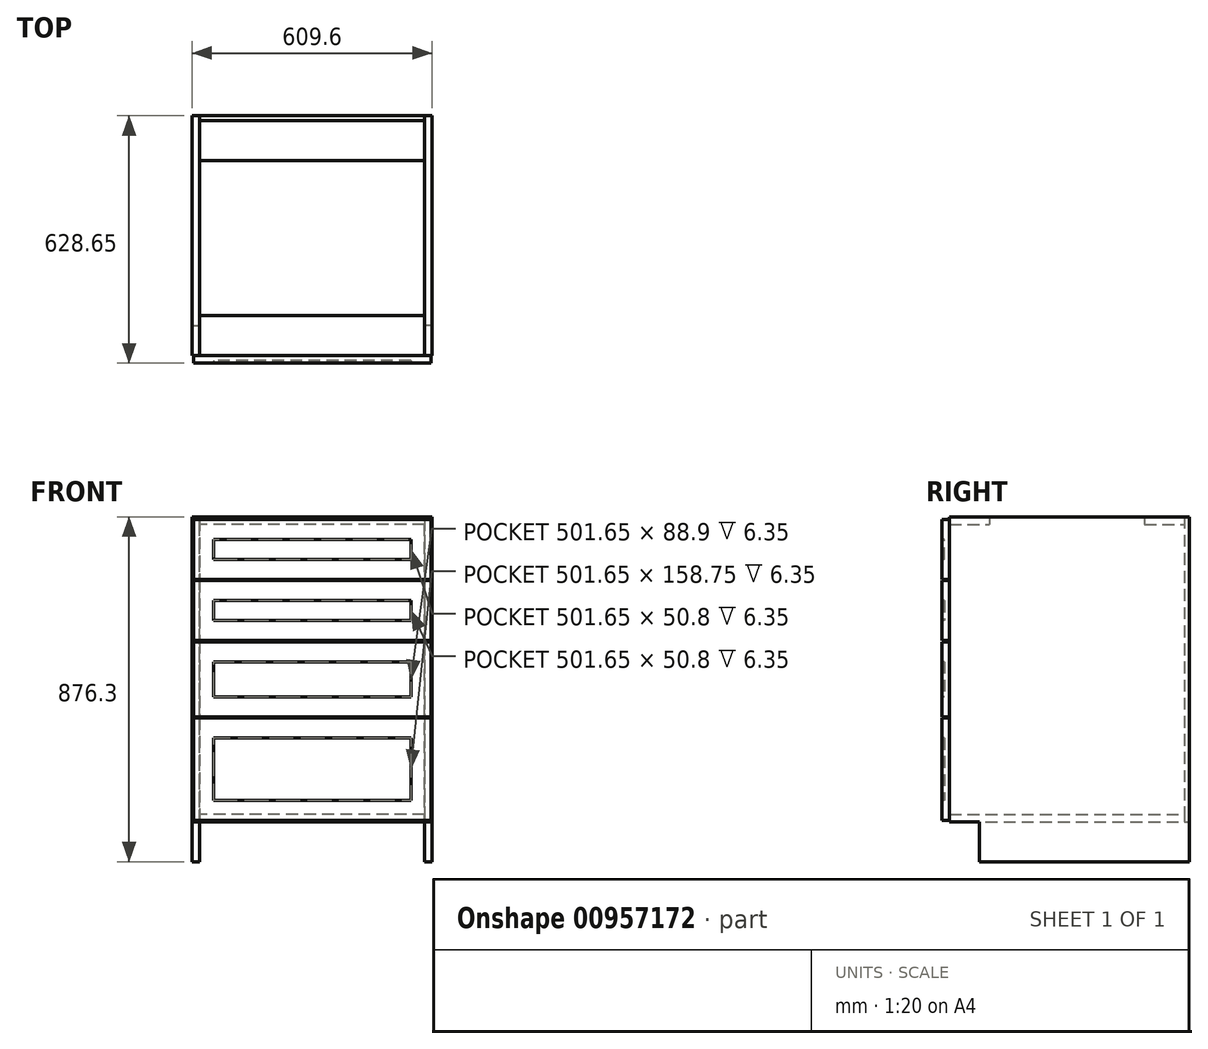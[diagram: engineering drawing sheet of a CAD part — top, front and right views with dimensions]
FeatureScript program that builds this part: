
annotation { "Feature Type Name" : "Feature", "Feature Type Description" : "" }
export const myFeature = defineFeature(function(context is Context, id is Id, definition is map)
    precondition{}
    {
        {
            var Q0;
            Q0=qCreatedBy(makeId("Right.planeOp"),FACE);
            var sketch = newSketch(context, id + "F0", { "sketchPlane" : qUnion([Q0])});
            skLineSegment(sketch, "E0", {"start": v(0, 0) * mm, "end": v(0, 876.3) * mm});
            skLineSegment(sketch, "E1", {"start": v(0, 876.3) * mm, "end": v(-609.6, 876.3) * mm});
            skLineSegment(sketch, "E2", {"start": v(-609.6, 876.3) * mm, "end": v(-609.6, 101.6) * mm});
            skLineSegment(sketch, "E3", {"start": v(-609.6, 101.6) * mm, "end": v(-533.4, 101.6) * mm});
            skLineSegment(sketch, "E4", {"start": v(-533.4, 101.6) * mm, "end": v(-533.4, 0) * mm});
            skLineSegment(sketch, "E5", {"start": v(-533.4, 0) * mm, "end": v(0, 0) * mm});
            skLineSegment(sketch, "E6", {"start": v(-609.6, 101.6) * mm, "end": v(-12.7, 101.6) * mm, "construction": true});
            skLineSegment(sketch, "E7", {"start": v(-12.7, 101.6) * mm, "end": v(-12.7, 120.65) * mm, "construction": true});
            skLineSegment(sketch, "E8", {"start": v(-12.7, 120.65) * mm, "end": v(-609.6, 120.65) * mm, "construction": true});
            skLineSegment(sketch, "E9", {"start": v(-552.45, 101.6) * mm, "end": v(-552.45, 0) * mm, "construction": true});
            skLineSegment(sketch, "E10", {"start": v(-552.45, 0) * mm, "end": v(-533.4, 0) * mm, "construction": true});
            skLineSegment(sketch, "E11", {"start": v(-12.7, 0) * mm, "end": v(-12.7, 876.3) * mm, "construction": true});
            skLineSegment(sketch, "E12", {"start": v(-12.7, 876.3) * mm, "end": v(-12.7, 857.25) * mm, "construction": true});
            skLineSegment(sketch, "E13", {"start": v(-12.7, 857.25) * mm, "end": v(-609.6, 857.25) * mm, "construction": true});
            skLineSegment(sketch, "E14", {"start": v(-609.6, 857.25) * mm, "end": v(-609.6, 876.3) * mm, "construction": true});
            skSolve(sketch);
        }
        {
            var Q0;
            Q0=qCreatedBy(makeId("Right.planeOp"),FACE);
            var sketch = newSketch(context, id + "F1", { "sketchPlane" : qUnion([Q0])});
            skLineSegment(sketch, "E15.bottom", {"start": v(-609.6, 120.65) * mm, "end": v(-12.7, 120.65) * mm});
            skLineSegment(sketch, "E15.top", {"start": v(-609.6, 101.6) * mm, "end": v(-12.7, 101.6) * mm});
            skLineSegment(sketch, "E15.left", {"start": v(-609.6, 120.65) * mm, "end": v(-609.6, 101.6) * mm});
            skLineSegment(sketch, "E15.right", {"start": v(-12.7, 120.65) * mm, "end": v(-12.7, 101.6) * mm});
            skLineSegment(sketch, "E16.bottom", {"start": v(-609.6, 876.3) * mm, "end": v(-508, 876.3) * mm});
            skLineSegment(sketch, "E16.top", {"start": v(-609.6, 857.25) * mm, "end": v(-508, 857.25) * mm});
            skLineSegment(sketch, "E16.left", {"start": v(-609.6, 876.3) * mm, "end": v(-609.6, 857.25) * mm});
            skLineSegment(sketch, "E16.right", {"start": v(-12.7, 876.3) * mm, "end": v(-12.7, 857.25) * mm});
            skLineSegment(sketch, "E17", {"start": v(-508, 876.3) * mm, "end": v(-508, 857.25) * mm});
            skLineSegment(sketch, "E18", {"start": v(-114.3, 876.3) * mm, "end": v(-114.3, 857.25) * mm});
            skLineSegment(sketch, "E19.trimOffspring", {"start": v(-114.3, 876.3) * mm, "end": v(-12.7, 876.3) * mm});
            skLineSegment(sketch, "E20.trimOffspring", {"start": v(-114.3, 857.25) * mm, "end": v(-12.7, 857.25) * mm});
            skSolve(sketch);
        }
        {
            var Q0;
            Q0 = qSketchRegion(id + "F1", true);
            extrude(context, id + "F2", {"entities" : qUnion([Q0]), "endBound" : BoundingType.SYMMETRIC, "depth" : 571.5 * mm, "offsetDistance" : 25.4 * mm});
        }
        {
            var Q0;
            Q0=makeQuery(id+"F2.opExtrude","CAP_FACE",FACE,{"disambiguationData":[OSD([sQuery(id+"F1.wireOp",EDGE,"E16.bottom"),sQuery(id+"F1.wireOp",EDGE,"E16.top"),sQuery(id+"F1.wireOp",EDGE,"E16.left"),sQuery(id+"F1.wireOp",EDGE,"E16.right")])],"isStart":false});
            var sketch = newSketch(context, id + "F3", { "sketchPlane" : qUnion([Q0])});
            skLineSegment(sketch, "E21", {"start": v(-609.6, 876.3) * mm, "end": v(-609.6, 101.6) * mm});
            skLineSegment(sketch, "E22", {"start": v(-609.6, 101.6) * mm, "end": v(-533.4, 101.6) * mm});
            skLineSegment(sketch, "E23", {"start": v(-533.4, 101.6) * mm, "end": v(-533.4, 0) * mm});
            skLineSegment(sketch, "E24", {"start": v(-533.4, 0) * mm, "end": v(0, 0) * mm});
            skLineSegment(sketch, "E25", {"start": v(0, 0) * mm, "end": v(0, 876.3) * mm});
            skLineSegment(sketch, "E26", {"start": v(0, 876.3) * mm, "end": v(-609.6, 876.3) * mm});
            skSolve(sketch);
        }
        {
            var Q0;
            Q0 = qSketchRegion(id + "F3", true);
            extrude(context, id + "F4", {"entities" : qUnion([Q0]), "depth" : 19.05 * mm, "offsetDistance" : 25.4 * mm});
        }
        {
            var Q0;
            Q0=makeQuery(id+"F4.opExtrude","SWEPT_BODY",BODY,{"disambiguationData":[OSD([sQuery(id+"F3.wireOp",EDGE,"E21"),sQuery(id+"F3.wireOp",EDGE,"E22"),sQuery(id+"F3.wireOp",EDGE,"E23"),sQuery(id+"F3.wireOp",EDGE,"E24"),sQuery(id+"F3.wireOp",EDGE,"E25"),sQuery(id+"F3.wireOp",EDGE,"E26")])]});
            var Q1;
            Q1=qCreatedBy(makeId("Right.planeOp"),FACE);
            mirror(context, id + "F5", {"entities" : qUnion([Q0]), "mirrorPlane" : qUnion([Q1])});
        }
        {
            var Q0;
            Q0=makeQuery(id+"F5.opPattern","COPY",FACE,{"derivedFrom":makeQuery(id+"F4.opExtrude","CAP_FACE",FACE,{"disambiguationData":[OSD([sQuery(id+"F3.wireOp",EDGE,"E21"),sQuery(id+"F3.wireOp",EDGE,"E22"),sQuery(id+"F3.wireOp",EDGE,"E23"),sQuery(id+"F3.wireOp",EDGE,"E24"),sQuery(id+"F3.wireOp",EDGE,"E25"),sQuery(id+"F3.wireOp",EDGE,"E26")])],"isStart":true}),"instanceName":"1"});
            var sketch = newSketch(context, id + "F6", { "sketchPlane" : qUnion([Q0])});
            skLineSegment(sketch, "E27.bottom", {"start": v(-12.7, 876.3) * mm, "end": v(0, 876.3) * mm});
            skLineSegment(sketch, "E27.top", {"start": v(-12.7, 101.6) * mm, "end": v(0, 101.6) * mm});
            skLineSegment(sketch, "E27.left", {"start": v(-12.7, 876.3) * mm, "end": v(-12.7, 101.6) * mm});
            skLineSegment(sketch, "E27.right", {"start": v(0, 876.3) * mm, "end": v(0, 101.6) * mm});
            skSolve(sketch);
        }
        {
            var Q0;
            Q0 = qSketchRegion(id + "F6", true);
            var Q1;
            Q1=makeQuery(id+"F4.opExtrude","SWEPT_BODY",BODY,{"disambiguationData":[OSD([sQuery(id+"F3.wireOp",EDGE,"E21"),sQuery(id+"F3.wireOp",EDGE,"E22"),sQuery(id+"F3.wireOp",EDGE,"E23"),sQuery(id+"F3.wireOp",EDGE,"E24"),sQuery(id+"F3.wireOp",EDGE,"E25"),sQuery(id+"F3.wireOp",EDGE,"E26")])]});
            extrude(context, id + "F7", {"entities" : qUnion([Q0]), "endBound" : BoundingType.UP_TO_BODY, "depth" : 25.4 * mm, "endBoundEntityBody" : qUnion([Q1]), "offsetDistance" : 25.4 * mm});
        }
        {
            var Q0;
            Q0=makeQuery(id+"F2.opExtrude","SWEPT_FACE",FACE,{"disambiguationData":[OSD([sQuery(id+"F1.wireOp",EDGE,"E16.left")])]});
            var sketch = newSketch(context, id + "F8", { "sketchPlane" : qUnion([Q0])});
            skLineSegment(sketch, "E28.bottom", {"start": v(-301.63, 869.95) * mm, "end": v(301.63, 869.95) * mm});
            skLineSegment(sketch, "E28.top", {"start": v(-301.63, 717.55) * mm, "end": v(301.63, 717.55) * mm});
            skLineSegment(sketch, "E28.left", {"start": v(-301.63, 869.95) * mm, "end": v(-301.63, 717.55) * mm});
            skLineSegment(sketch, "E28.right", {"start": v(301.63, 869.95) * mm, "end": v(301.63, 717.55) * mm});
            skLineSegment(sketch, "E29.bottom", {"start": v(-301.63, 714.38) * mm, "end": v(301.63, 714.38) * mm});
            skLineSegment(sketch, "E29.top", {"start": v(-301.63, 561.98) * mm, "end": v(301.63, 561.98) * mm});
            skLineSegment(sketch, "E29.left", {"start": v(-301.63, 714.38) * mm, "end": v(-301.63, 561.98) * mm});
            skLineSegment(sketch, "E29.right", {"start": v(301.63, 714.38) * mm, "end": v(301.63, 561.98) * mm});
            skLineSegment(sketch, "E30.bottom", {"start": v(-301.62, 558.8) * mm, "end": v(301.63, 558.8) * mm});
            skLineSegment(sketch, "E30.top", {"start": v(-301.62, 368.3) * mm, "end": v(301.63, 368.3) * mm});
            skLineSegment(sketch, "E30.left", {"start": v(-301.63, 558.8) * mm, "end": v(-301.62, 368.3) * mm});
            skLineSegment(sketch, "E30.right", {"start": v(301.63, 558.8) * mm, "end": v(301.63, 368.3) * mm});
            skLineSegment(sketch, "E31.bottom", {"start": v(-301.62, 365.12) * mm, "end": v(301.63, 365.12) * mm});
            skLineSegment(sketch, "E31.top", {"start": v(-301.62, 104.78) * mm, "end": v(301.63, 104.78) * mm});
            skLineSegment(sketch, "E31.left", {"start": v(-301.62, 365.12) * mm, "end": v(-301.62, 104.78) * mm});
            skLineSegment(sketch, "E31.right", {"start": v(301.63, 365.12) * mm, "end": v(301.63, 104.78) * mm});
            skLineSegment(sketch, "E32", {"start": v(0, 876.3) * mm, "end": v(0, 869.95) * mm, "construction": true});
            skLineSegment(sketch, "E33.bottom", {"start": v(-285.75, 725.49) * mm, "end": v(285.75, 725.49) * mm, "construction": true});
            skLineSegment(sketch, "E33.top", {"start": v(-285.75, 706.44) * mm, "end": v(285.75, 706.44) * mm, "construction": true});
            skLineSegment(sketch, "E33.left", {"start": v(-285.75, 725.49) * mm, "end": v(-285.75, 706.44) * mm, "construction": true});
            skLineSegment(sketch, "E33.right", {"start": v(285.75, 725.49) * mm, "end": v(285.75, 706.44) * mm, "construction": true});
            skLineSegment(sketch, "E34.bottom", {"start": v(285.75, 569.91) * mm, "end": v(-285.75, 569.91) * mm, "construction": true});
            skLineSegment(sketch, "E34.top", {"start": v(285.75, 550.86) * mm, "end": v(-285.75, 550.86) * mm, "construction": true});
            skLineSegment(sketch, "E34.left", {"start": v(285.75, 569.91) * mm, "end": v(285.75, 550.86) * mm, "construction": true});
            skLineSegment(sketch, "E34.right", {"start": v(-285.75, 569.91) * mm, "end": v(-285.75, 550.86) * mm, "construction": true});
            skLineSegment(sketch, "E35.bottom", {"start": v(-285.75, 376.24) * mm, "end": v(285.75, 376.24) * mm, "construction": true});
            skLineSegment(sketch, "E35.top", {"start": v(-285.75, 357.19) * mm, "end": v(285.75, 357.19) * mm, "construction": true});
            skLineSegment(sketch, "E35.left", {"start": v(-285.75, 376.24) * mm, "end": v(-285.75, 357.19) * mm, "construction": true});
            skLineSegment(sketch, "E35.right", {"start": v(285.75, 376.24) * mm, "end": v(285.75, 357.19) * mm, "construction": true});
            skLineSegment(sketch, "E36", {"start": v(-301.63, 717.55) * mm, "end": v(-301.63, 714.38) * mm, "construction": true});
            skLineSegment(sketch, "E37", {"start": v(-285.75, 715.96) * mm, "end": v(-301.63, 715.96) * mm, "construction": true});
            skLineSegment(sketch, "E38", {"start": v(-301.62, 368.3) * mm, "end": v(-301.62, 365.12) * mm, "construction": true});
            skLineSegment(sketch, "E39", {"start": v(-285.75, 366.71) * mm, "end": v(-301.62, 366.71) * mm, "construction": true});
            skLineSegment(sketch, "E40", {"start": v(-301.63, 561.98) * mm, "end": v(-301.63, 558.8) * mm, "construction": true});
            skLineSegment(sketch, "E41", {"start": v(-285.75, 560.39) * mm, "end": v(-301.63, 560.39) * mm, "construction": true});
            skSolve(sketch);
        }
        {
            var Q0;
            Q0 = qSketchRegion(id + "F8", true);
            extrude(context, id + "F9", {"entities" : qUnion([Q0]), "depth" : 19.05 * mm, "offsetDistance" : 25.4 * mm});
        }
        {
            var Q0;
            Q0=makeQuery(id+"F9.opExtrude","CAP_FACE",FACE,{"disambiguationData":[OSD([sQuery(id+"F8.wireOp",EDGE,"E28.bottom"),sQuery(id+"F8.wireOp",EDGE,"E28.top"),sQuery(id+"F8.wireOp",EDGE,"E28.left"),sQuery(id+"F8.wireOp",EDGE,"E28.right")])],"isStart":false});
            var sketch = newSketch(context, id + "F10", { "sketchPlane" : qUnion([Q0])});
            skLineSegment(sketch, "E42.0", {"start": v(250.83, 819.15) * mm, "end": v(-250.83, 819.15) * mm});
            skLineSegment(sketch, "E42.1", {"start": v(250.83, 768.35) * mm, "end": v(250.83, 819.15) * mm});
            skLineSegment(sketch, "E42.2", {"start": v(-250.83, 768.35) * mm, "end": v(250.83, 768.35) * mm});
            skLineSegment(sketch, "E42.3", {"start": v(-250.83, 819.15) * mm, "end": v(-250.83, 768.35) * mm});
            skLineSegment(sketch, "E43.0", {"start": v(-250.83, 663.58) * mm, "end": v(-250.83, 612.78) * mm});
            skLineSegment(sketch, "E43.1", {"start": v(250.83, 663.58) * mm, "end": v(-250.83, 663.58) * mm});
            skLineSegment(sketch, "E43.2", {"start": v(250.83, 612.78) * mm, "end": v(250.83, 663.58) * mm});
            skLineSegment(sketch, "E43.3", {"start": v(-250.83, 612.78) * mm, "end": v(250.83, 612.78) * mm});
            skLineSegment(sketch, "E44.0", {"start": v(-250.82, 508) * mm, "end": v(-250.82, 419.1) * mm});
            skLineSegment(sketch, "E44.1", {"start": v(250.83, 508) * mm, "end": v(-250.82, 508) * mm});
            skLineSegment(sketch, "E44.2", {"start": v(250.83, 419.1) * mm, "end": v(250.83, 508) * mm});
            skLineSegment(sketch, "E44.3", {"start": v(-250.82, 419.1) * mm, "end": v(250.83, 419.1) * mm});
            skLineSegment(sketch, "E45.0", {"start": v(-250.82, 314.32) * mm, "end": v(-250.82, 155.58) * mm});
            skLineSegment(sketch, "E45.1", {"start": v(250.83, 314.32) * mm, "end": v(-250.82, 314.32) * mm});
            skLineSegment(sketch, "E45.2", {"start": v(250.83, 155.58) * mm, "end": v(250.83, 314.32) * mm});
            skLineSegment(sketch, "E45.3", {"start": v(-250.82, 155.58) * mm, "end": v(250.83, 155.58) * mm});
            skSolve(sketch);
        }
        {
            var Q0;
            Q0 = qSketchRegion(id + "F10", true);
            extrude(context, id + "F11", {"entities" : qUnion([Q0]), "operationType" : NewBodyOperationType.REMOVE, "oppositeDirection" : true, "depth" : 6.35 * mm, "offsetDistance" : 25.4 * mm});
        }
    });
